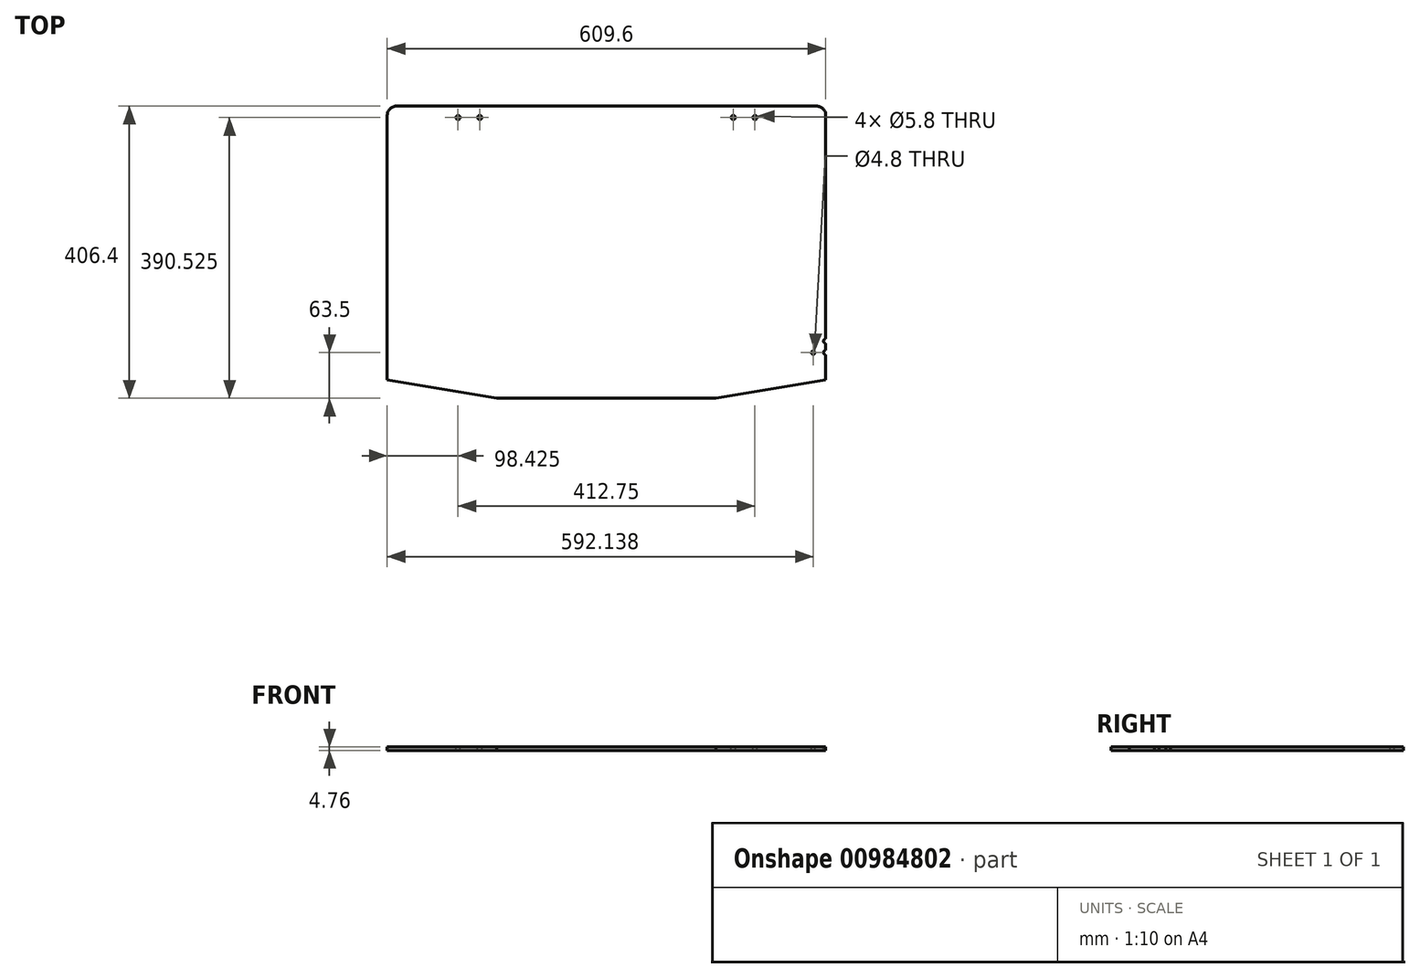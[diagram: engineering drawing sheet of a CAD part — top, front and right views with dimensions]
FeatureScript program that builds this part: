
annotation { "Feature Type Name" : "Feature", "Feature Type Description" : "" }
export const myFeature = defineFeature(function(context is Context, id is Id, definition is map)
    precondition{}
    {
        {
            var Q0;
            Q0=qCreatedBy(makeId("Top.planeOp"),FACE);
            var sketch = newSketch(context, id + "F0", { "sketchPlane" : qUnion([Q0])});
            skLineSegment(sketch, "E0.bottom", {"start": v(304.8, -203.2) * mm, "end": v(-304.8, -203.2) * mm});
            skLineSegment(sketch, "E0.top", {"start": v(304.8, 203.2) * mm, "end": v(-304.8, 203.2) * mm});
            skLineSegment(sketch, "E0.left", {"start": v(304.8, -203.2) * mm, "end": v(304.8, 203.2) * mm});
            skLineSegment(sketch, "E0.right", {"start": v(-304.8, -203.2) * mm, "end": v(-304.8, 203.2) * mm});
            skPoint(sketch, "E0.middle", {"position": v(0, 0) * mm});
            skSolve(sketch);
        }
        {
            var Q0;
            Q0 = qSketchRegion(id + "F0", true);
            extrude(context, id + "F1", {"entities" : qUnion([Q0]), "depth" : 4.76 * mm, "offsetDistance" : 25.4 * mm});
        }
        {
            var Q0;
            Q0=makeQuery(id+"F1.opExtrude","CAP_FACE",FACE,{"disambiguationData":[OSD([sQuery(id+"F0.wireOp",EDGE,"E0.bottom"),sQuery(id+"F0.wireOp",EDGE,"E0.top"),sQuery(id+"F0.wireOp",EDGE,"E0.left"),sQuery(id+"F0.wireOp",EDGE,"E0.right")])],"isStart":false});
            var sketch = newSketch(context, id + "F2", { "sketchPlane" : qUnion([Q0])});
            skLineSegment(sketch, "E1", {"start": v(0, 203.2) * mm, "end": v(0, -203.2) * mm, "construction": true});
            skLineSegment(sketch, "E2", {"start": v(-304.8, -177.8) * mm, "end": v(-152.4, -203.2) * mm});
            skLineSegment(sketch, "E3", {"start": v(-152.4, -203.2) * mm, "end": v(-304.8, -203.2) * mm});
            skLineSegment(sketch, "E4", {"start": v(-304.8, -203.2) * mm, "end": v(-304.8, -177.8) * mm});
            skLineSegment(sketch, "E5.MirrorCS", {"start": v(304.8, -203.2) * mm, "end": v(304.8, -177.8) * mm});
            skLineSegment(sketch, "E6.MirrorCS", {"start": v(304.8, -177.8) * mm, "end": v(152.4, -203.2) * mm});
            skLineSegment(sketch, "E7.MirrorCS", {"start": v(152.4, -203.2) * mm, "end": v(304.8, -203.2) * mm});
            skSolve(sketch);
        }
        {
            var Q0;
            Q0 = qSketchRegion(id + "F2", true);
            extrude(context, id + "F3", {"entities" : qUnion([Q0]), "operationType" : NewBodyOperationType.REMOVE, "oppositeDirection" : true, "depth" : 25.4 * mm, "offsetDistance" : 25.4 * mm});
        }
        {
            var Q0;
            Q0=makeQuery(id+"F1.opExtrude","CAP_FACE",FACE,{"disambiguationData":[OSD([sQuery(id+"F0.wireOp",EDGE,"E0.bottom"),sQuery(id+"F0.wireOp",EDGE,"E0.top"),sQuery(id+"F0.wireOp",EDGE,"E0.left"),sQuery(id+"F0.wireOp",EDGE,"E0.right")])],"isStart":false});
            var sketch = newSketch(context, id + "F4", { "sketchPlane" : qUnion([Q0])});
            skLineSegment(sketch, "E8", {"start": v(0, -203.2) * mm, "end": v(0, 203.2) * mm, "construction": true});
            skPoint(sketch, "E9", {"position": v(-206.37, 187.32) * mm});
            skPoint(sketch, "E10", {"position": v(-176.21, 187.32) * mm});
            skPoint(sketch, "E11.MirrorP", {"position": v(176.21, 187.33) * mm});
            skPoint(sketch, "E12.MirrorP", {"position": v(206.38, 187.33) * mm});
            skSolve(sketch);
        }
        {
            var Q0;
            Q0=sQuery(id+"F4.wireOp",VERTEX,"E9");
            var Q1;
            Q1=sQuery(id+"F4.wireOp",VERTEX,"E10");
            var Q2;
            Q2=sQuery(id+"F4.wireOp",VERTEX,"E11.MirrorP");
            var Q3;
            Q3=sQuery(id+"F4.wireOp",VERTEX,"E12.MirrorP");
            var Q4;
            Q4=makeQuery(id+"F1.opExtrude","SWEPT_BODY",BODY,{"disambiguationData":[OSD([sQuery(id+"F0.wireOp",EDGE,"E0.bottom"),sQuery(id+"F0.wireOp",EDGE,"E0.top"),sQuery(id+"F0.wireOp",EDGE,"E0.left"),sQuery(id+"F0.wireOp",EDGE,"E0.right")])]});
            hole(context, id + "F5", {"style" : HoleStyle.SIMPLE, "endStyle" : HoleEndStyle.THROUGH, "standardTappedOrClearance" : lookupTablePath({ "fit" : "Loose", "standard" : "ISO", "size" : "M5", "type" : "Clearance" }), "standardBlindInLast" : lookupTablePath({ "fit" : "Loose", "standard" : "ISO", "engagement" : "75%", "pitch" : "0.8 mm", "size" : "M5", "type" : "Clearance & tapped" }), "holeDiameter" : 5.8 * mm, "majorDiameter" : 6.35 * mm, "isTappedThrough" : true, "tappedDepth" : 23.02 * mm, "tapClearance" : 3, "locations" : qUnion([Q0, Q1, Q2, Q3]), "scope" : qUnion([Q4])});
        }
        {
            var Q0;
            Q0=makeQuery(id+"F1.opExtrude","CAP_FACE",FACE,{"disambiguationData":[OSD([sQuery(id+"F0.wireOp",EDGE,"E0.bottom"),sQuery(id+"F0.wireOp",EDGE,"E0.top"),sQuery(id+"F0.wireOp",EDGE,"E0.left"),sQuery(id+"F0.wireOp",EDGE,"E0.right")])],"isStart":false});
            var sketch = newSketch(context, id + "F6", { "sketchPlane" : qUnion([Q0])});
            skArc(sketch, "E13", {"start": v(304.8, -120.65) * mm, "mid": v(301.63, -123.82) * mm, "end": v(304.8, -127) * mm});
            skArc(sketch, "E14", {"start": v(304.8, -136.53) * mm, "mid": v(301.63, -139.7) * mm, "end": v(304.8, -142.88) * mm});
            skLineSegment(sketch, "E15", {"start": v(304.8, -120.65) * mm, "end": v(304.8, -127) * mm});
            skLineSegment(sketch, "E16", {"start": v(304.8, -136.53) * mm, "end": v(304.8, -142.88) * mm});
            skSolve(sketch);
        }
        {
            var Q0;
            Q0 = qSketchRegion(id + "F6", true);
            extrude(context, id + "F7", {"entities" : qUnion([Q0]), "operationType" : NewBodyOperationType.REMOVE, "oppositeDirection" : true, "depth" : 25.4 * mm, "offsetDistance" : 25.4 * mm});
        }
        {
            var Q0;
            Q0=makeQuery(id+"F1.opExtrude","CAP_FACE",FACE,{"disambiguationData":[OSD([sQuery(id+"F0.wireOp",EDGE,"E0.bottom"),sQuery(id+"F0.wireOp",EDGE,"E0.top"),sQuery(id+"F0.wireOp",EDGE,"E0.left"),sQuery(id+"F0.wireOp",EDGE,"E0.right")])],"isStart":false});
            var sketch = newSketch(context, id + "F8", { "sketchPlane" : qUnion([Q0])});
            skPoint(sketch, "E17", {"position": v(287.34, -139.7) * mm});
            skSolve(sketch);
        }
        {
            var Q0;
            Q0=sQuery(id+"F8.wireOp",VERTEX,"E17");
            var Q1;
            Q1=makeQuery(id+"F1.opExtrude","SWEPT_BODY",BODY,{"disambiguationData":[OSD([sQuery(id+"F0.wireOp",EDGE,"E0.bottom"),sQuery(id+"F0.wireOp",EDGE,"E0.top"),sQuery(id+"F0.wireOp",EDGE,"E0.left"),sQuery(id+"F0.wireOp",EDGE,"E0.right")])]});
            hole(context, id + "F9", {"style" : HoleStyle.SIMPLE, "endStyle" : HoleEndStyle.THROUGH, "standardTappedOrClearance" : lookupTablePath({ "fit" : "Loose", "standard" : "ISO", "size" : "M4", "type" : "Clearance" }), "standardBlindInLast" : lookupTablePath({ "fit" : "Loose", "standard" : "ISO", "engagement" : "75%", "pitch" : "0.7 mm", "size" : "M4", "type" : "Clearance & tapped" }), "holeDiameter" : 4.8 * mm, "majorDiameter" : 6.35 * mm, "isTappedThrough" : true, "tappedDepth" : 23.02 * mm, "tapClearance" : 3, "locations" : qUnion([Q0]), "scope" : qUnion([Q1])});
        }
        {
            var Q0;
            Q0=makeQuery(id+"F3.boolean.opBoolean","COPY",EDGE,{"derivedFrom":makeQuery(id+"F3.opExtrude","SWEPT_EDGE",EDGE,{"disambiguationData":[OSD([sQuery(id+"F0.wireOp",EDGE,"E0.left"),sQuery(id+"F2.wireOp",EDGE,"E5.MirrorCS"),sQuery(id+"F2.wireOp",EDGE,"E6.MirrorCS")])]})});
            var Q1;
            Q1=makeQuery(id+"F3.boolean.opBoolean","COPY",EDGE,{"derivedFrom":makeQuery(id+"F3.opExtrude","SWEPT_EDGE",EDGE,{"disambiguationData":[OSD([sQuery(id+"F0.wireOp",EDGE,"E0.right"),sQuery(id+"F2.wireOp",EDGE,"E2"),sQuery(id+"F2.wireOp",EDGE,"E4")])]})});
            var Q2;
            Q2=makeQuery(id+"F1.opExtrude","SWEPT_EDGE",EDGE,{"disambiguationData":[OSD([sQuery(id+"F0.wireOp",EDGE,"E0.top"),sQuery(id+"F0.wireOp",EDGE,"E0.left")])]});
            var Q3;
            Q3=makeQuery(id+"F1.opExtrude","SWEPT_EDGE",EDGE,{"disambiguationData":[OSD([sQuery(id+"F0.wireOp",EDGE,"E0.top"),sQuery(id+"F0.wireOp",EDGE,"E0.right")])]});
            fillet(context, id + "F10", {"entities" : qUnion([Q0, Q1, Q2, Q3]), "tangentPropagation" : true, "radius" : 12.7 * mm, "defaultsChanged" : false, "vertexSettings" : [], "allowEdgeOverflow" : false});
        }
    });
